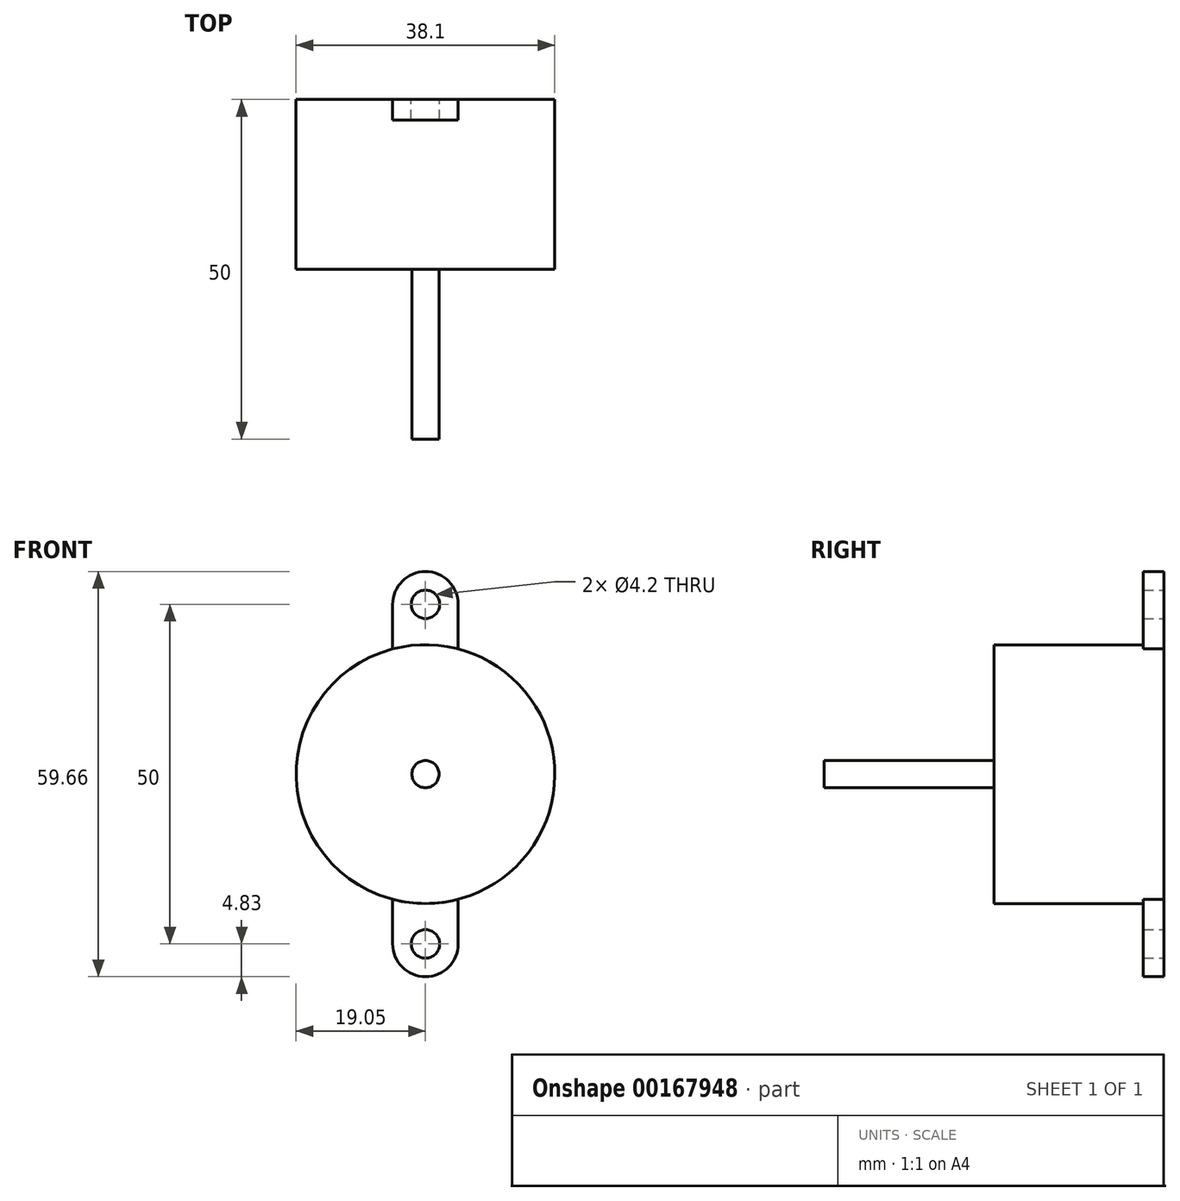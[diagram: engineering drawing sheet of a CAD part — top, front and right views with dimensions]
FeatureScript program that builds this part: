
annotation { "Feature Type Name" : "Feature", "Feature Type Description" : "" }
export const myFeature = defineFeature(function(context is Context, id is Id, definition is map)
    precondition{}
    {
        {
            var Q0;
            Q0=qCreatedBy(makeId("Front.planeOp"),FACE);
            cPlane(context, id + "F0", {"entities" : qUnion([Q0]), "cplaneType" : CPlaneType.OFFSET, "offset" : 0 * mm, "width" : 150 * mm, "height" : 150 * mm});
        }
        {
            var Q0;
            Q0=qCreatedBy(id+"F0.planeOp",FACE);
            var sketch = newSketch(context, id + "F1", { "sketchPlane" : qUnion([Q0])});
            skCircle(sketch, "E0", {"center": v(0, 0) * mm, "radius": 19.05 * mm});
            skSolve(sketch);
        }
        {
            var Q0;
            Q0 = qSketchRegion(id + "F1", true);
            extrude(context, id + "F2", {"entities" : qUnion([Q0]), "depth" : 25 * mm});
        }
        {
            var Q0;
            Q0=qCreatedBy(id+"F0.planeOp",FACE);
            var sketch = newSketch(context, id + "F3", { "sketchPlane" : qUnion([Q0])});
            skLineSegment(sketch, "E1", {"start": v(0, 55.28) * mm, "end": v(0, -53.48) * mm, "construction": true});
            skLineSegment(sketch, "E2", {"start": v(-52.41, 0) * mm, "end": v(61.28, 0) * mm, "construction": true});
            skCircle(sketch, "E3", {"center": v(0, 25) * mm, "radius": 2.1 * mm});
            skLineSegment(sketch, "E4.left", {"start": v(-4.83, 25) * mm, "end": v(-4.83, 18.43) * mm});
            skLineSegment(sketch, "E4.right", {"start": v(4.83, 25) * mm, "end": v(4.83, 18.43) * mm});
            skArc(sketch, "E5", {"start": v(4.83, 25) * mm, "mid": v(0, 29.83) * mm, "end": v(-4.83, 25) * mm});
            skArc(sketch, "E6.trimOffspring", {"start": v(4.83, 18.43) * mm, "mid": v(0, 19.05) * mm, "end": v(-4.83, 18.43) * mm});
            skCircle(sketch, "E7.MirrorC", {"center": v(0, -25) * mm, "radius": 2.1 * mm});
            skLineSegment(sketch, "E8.MirrorCS", {"start": v(4.83, -25) * mm, "end": v(4.83, -18.43) * mm});
            skLineSegment(sketch, "E9.MirrorCS", {"start": v(-4.83, -25) * mm, "end": v(-4.83, -18.43) * mm});
            skArc(sketch, "E10.MirrorCS", {"start": v(4.83, -25) * mm, "mid": v(0, -29.83) * mm, "end": v(-4.83, -25) * mm});
            skArc(sketch, "E11.MirrorCS", {"start": v(4.83, -18.43) * mm, "mid": v(0, -19.05) * mm, "end": v(-4.83, -18.43) * mm});
            skSolve(sketch);
        }
        {
            var Q0;
            Q0 = qSketchRegion(id + "F3", true);
            extrude(context, id + "F4", {"entities" : qUnion([Q0]), "operationType" : NewBodyOperationType.ADD, "depth" : 3 * mm});
        }
        {
            var Q0;
            Q0=makeQuery(id+"F2.opExtrude","CAP_FACE",FACE,{"disambiguationData":[OSD([sQuery(id+"F1.wireOp",EDGE,"E0")])],"isStart":false});
            var sketch = newSketch(context, id + "F5", { "sketchPlane" : qUnion([Q0])});
            skCircle(sketch, "E12", {"center": v(0, 0) * mm, "radius": 2 * mm});
            skSolve(sketch);
        }
        {
            var Q0;
            Q0 = qSketchRegion(id + "F5", true);
            extrude(context, id + "F6", {"entities" : qUnion([Q0]), "operationType" : NewBodyOperationType.ADD, "depth" : 25 * mm});
        }
    });
